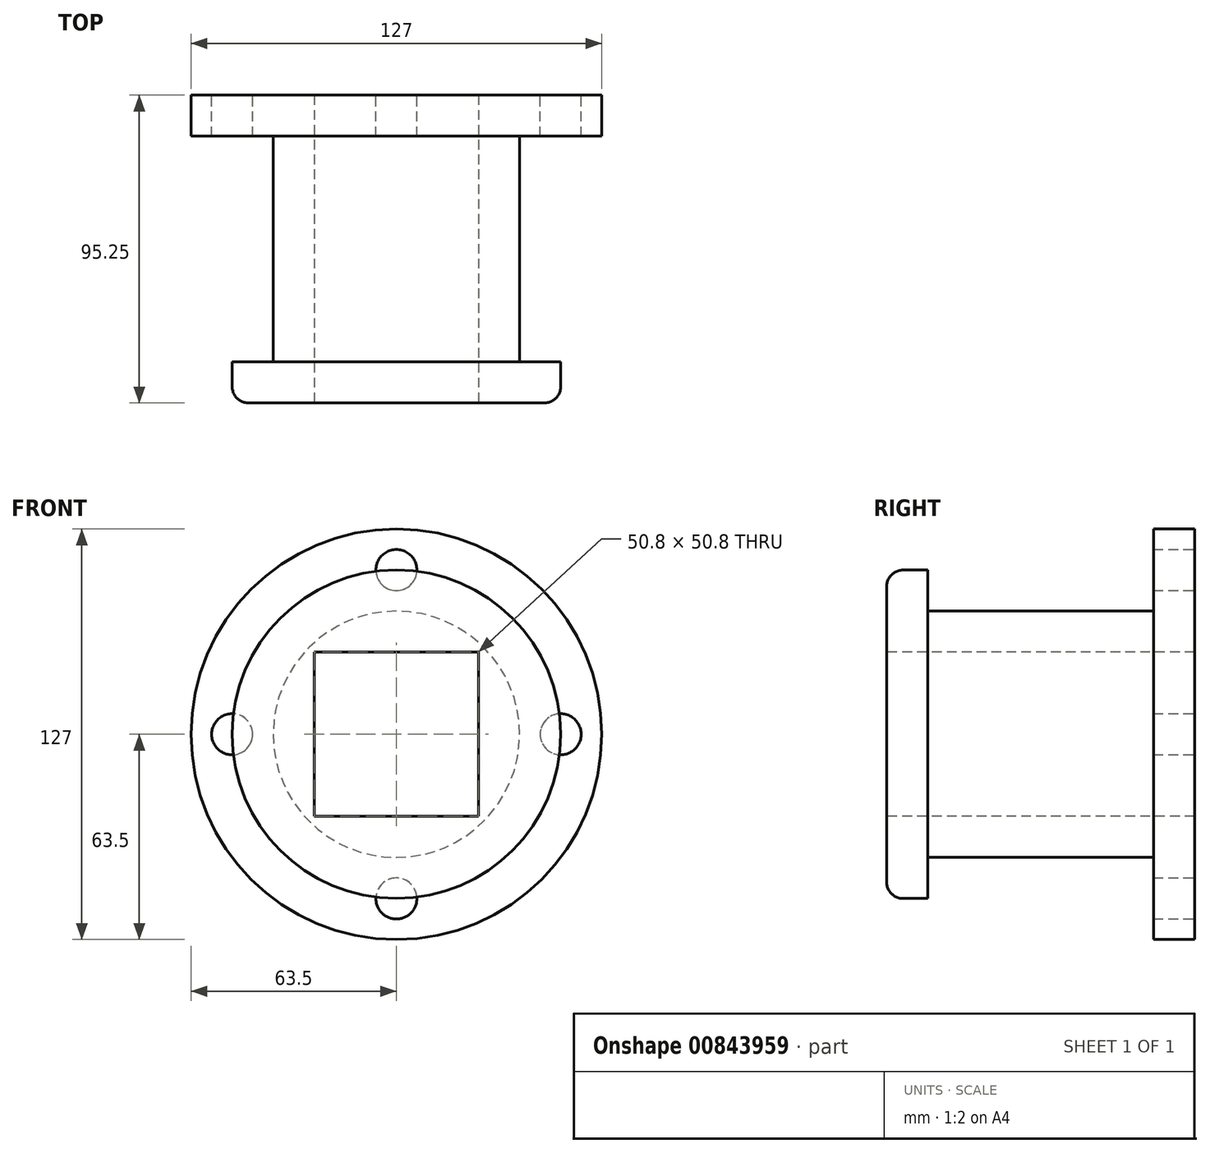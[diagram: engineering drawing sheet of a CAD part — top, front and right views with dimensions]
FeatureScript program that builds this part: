
annotation { "Feature Type Name" : "Feature", "Feature Type Description" : "" }
export const myFeature = defineFeature(function(context is Context, id is Id, definition is map)
    precondition{}
    {
        {
            var Q0;
            Q0=qCreatedBy(makeId("Front.planeOp"),FACE);
            var sketch = newSketch(context, id + "F0", { "sketchPlane" : qUnion([Q0])});
            skCircle(sketch, "E0", {"center": v(0, 0) * mm, "radius": 63.5 * mm});
            skPoint(sketch, "E1.center.orphan", {"position": v(0, -55.28) * mm});
            skPoint(sketch, "E2.center.orphan", {"position": v(0, 52.07) * mm});
            skPoint(sketch, "E3.center.orphan", {"position": v(52.07, 0) * mm});
            skPoint(sketch, "E4.center.orphan", {"position": v(0, -52.07) * mm});
            skPoint(sketch, "E5.center.orphan", {"position": v(-52.07, 0) * mm});
            skCircle(sketch, "E6", {"center": v(-50.8, 0) * mm, "radius": 6.35 * mm});
            skCircle(sketch, "E7", {"center": v(0, 50.8) * mm, "radius": 6.35 * mm});
            skCircle(sketch, "E8", {"center": v(50.8, 0) * mm, "radius": 6.35 * mm});
            skCircle(sketch, "E9", {"center": v(0, -50.8) * mm, "radius": 6.35 * mm});
            skSolve(sketch);
        }
        {
            var Q0;
            Q0 = qSketchRegion(id + "F0", true);
            extrude(context, id + "F1", {"entities" : qUnion([Q0]), "depth" : 12.7 * mm, "offsetDistance" : 25.4 * mm});
        }
        {
            var Q0;
            Q0=makeQuery(id+"F1.opExtrude","CAP_FACE",FACE,{"disambiguationData":[OSD([sQuery(id+"F0.wireOp",EDGE,"E0"),sQuery(id+"F0.wireOp",EDGE,"E5"),sQuery(id+"F0.wireOp",EDGE,"E2"),sQuery(id+"F0.wireOp",EDGE,"E3"),sQuery(id+"F0.wireOp",EDGE,"E4")])],"isStart":false});
            var sketch = newSketch(context, id + "F2", { "sketchPlane" : qUnion([Q0])});
            skCircle(sketch, "E10", {"center": v(0, 0) * mm, "radius": 38.1 * mm});
            skSolve(sketch);
        }
        {
            var Q0;
            Q0 = qSketchRegion(id + "F2", true);
            extrude(context, id + "F3", {"entities" : qUnion([Q0]), "operationType" : NewBodyOperationType.ADD, "depth" : 69.85 * mm, "offsetDistance" : 25.4 * mm});
        }
        {
            var Q0;
            Q0=makeQuery(id+"F3.opExtrude","CAP_FACE",FACE,{"disambiguationData":[OSD([sQuery(id+"F2.wireOp",EDGE,"E10")])],"isStart":false});
            var sketch = newSketch(context, id + "F4", { "sketchPlane" : qUnion([Q0])});
            skCircle(sketch, "E11", {"center": v(0, 0) * mm, "radius": 50.8 * mm});
            skSolve(sketch);
        }
        {
            var Q0;
            Q0 = qSketchRegion(id + "F4", true);
            extrude(context, id + "F5", {"entities" : qUnion([Q0]), "operationType" : NewBodyOperationType.ADD, "depth" : 12.7 * mm, "offsetDistance" : 25.4 * mm});
        }
        {
            var Q0;
            Q0=makeQuery(id+"F5.opExtrude","CAP_EDGE",EDGE,{"disambiguationData":[OSD([sQuery(id+"F4.wireOp",EDGE,"E11")])],"isStart":false});
            fillet(context, id + "F6", {"entities" : qUnion([Q0]), "radius" : 5.08 * mm, "tangentPropagation" : true, "allowEdgeOverflow" : false});
        }
        {
            var Q0;
            Q0=makeQuery(id+"F5.opExtrude","CAP_FACE",FACE,{"disambiguationData":[OSD([sQuery(id+"F4.wireOp",EDGE,"E11")])],"isStart":false});
            var sketch = newSketch(context, id + "F7", { "sketchPlane" : qUnion([Q0])});
            skLineSegment(sketch, "E12.bottom", {"start": v(-25.4, 25.4) * mm, "end": v(25.4, 25.4) * mm});
            skLineSegment(sketch, "E12.top", {"start": v(-25.4, -25.4) * mm, "end": v(25.4, -25.4) * mm});
            skLineSegment(sketch, "E12.left", {"start": v(-25.4, 25.4) * mm, "end": v(-25.4, -25.4) * mm});
            skLineSegment(sketch, "E12.right", {"start": v(25.4, 25.4) * mm, "end": v(25.4, -25.4) * mm});
            skSolve(sketch);
        }
        {
            var Q0;
            Q0=makeQuery(id+"F7.imprint","IMPRINT",FACE,{"disambiguationData":[TD([[makeQuery(id+"F7.imprint","IMPRINT",EDGE,{"derivedFrom":sQuery(id+"F7.wireOp",EDGE,"E12.bottom")}),-1.0]])]});
            extrude(context, id + "F8", {"entities" : qUnion([Q0]), "operationType" : NewBodyOperationType.REMOVE, "oppositeDirection" : true, "depth" : 101.6 * mm, "offsetDistance" : 25.4 * mm});
        }
    });
